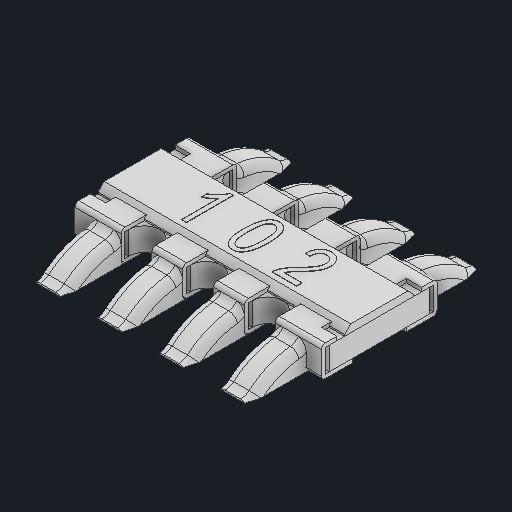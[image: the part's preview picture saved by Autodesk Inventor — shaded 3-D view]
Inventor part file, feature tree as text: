
AUTODESK INVENTOR PART (.ipt)
format: ipt  version: 2023 (Build 270158000, 158)  size: 499,712 bytes
history: native  units: in
note: dims shown in document units (in); Inventor stores cm internally (conversion verified against a paired STEP export)
features: other x8, fillet x2
ambient origin geometry x8: Origin, YZ Plane, XZ Plane, XY Plane, X Axis, Y Axis, Z Axis, Center Point
bodies: Solid1 (feature_tree), Solid2 (feature_tree), Solid3 (feature_tree), Solid4 (feature_tree), Solid5 (feature_tree), Solid6 (feature_tree), Solid7 (feature_tree), Solid8 (feature_tree), Solid9 (feature_tree), Solid10 (feature_tree)
feature tree (10):
  other  "Cut-Extrude7"
  other  "Boss-Extrude5"
  fillet  "Fillet2"  [1 undecoded]
  fillet  "Fillet1"  [1 undecoded]
  other  "LPattern3[1]"
  other  "LPattern3[2]"
  other  "LPattern3[3]"
  other  "LPattern3[4]"
  other  "LPattern3[5]"
  other  "LPattern3[6]"
note: 2 required parameter values undecoded (feature->parameter linkage not recoverable at this tier; creation-order binding heuristic only, values carry confidence <= 0.55)
